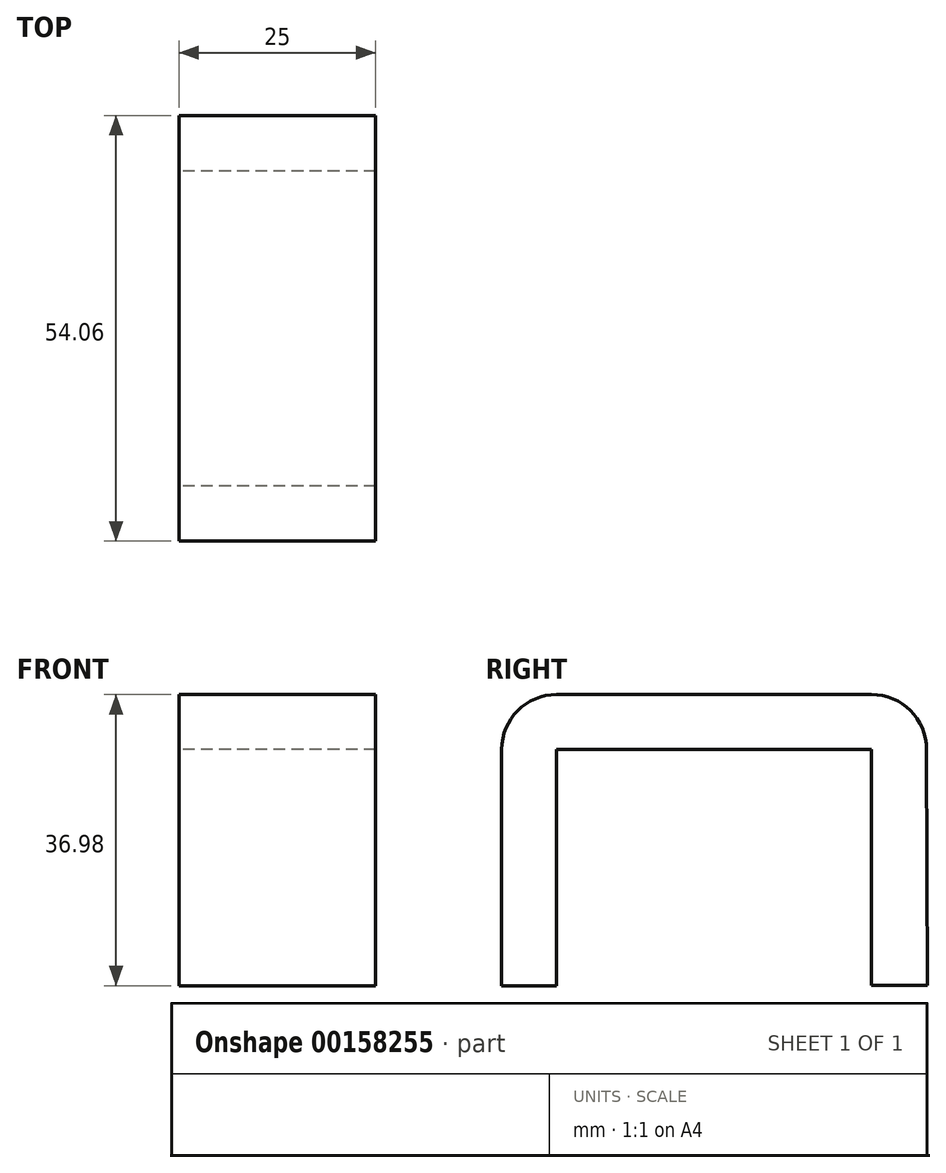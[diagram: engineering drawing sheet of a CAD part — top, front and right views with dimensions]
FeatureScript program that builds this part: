
annotation { "Feature Type Name" : "Feature", "Feature Type Description" : "" }
export const myFeature = defineFeature(function(context is Context, id is Id, definition is map)
    precondition{}
    {
        {
            var Q0;
            Q0=qCreatedBy(makeId("Right.planeOp"),FACE);
            var sketch = newSketch(context, id + "F0", { "sketchPlane" : qUnion([Q0])});
            skLineSegment(sketch, "E0", {"start": v(-27, 2.82) * mm, "end": v(-27, -27.18) * mm});
            skArc(sketch, "E1", {"start": v(-27, 2.82) * mm, "mid": v(-24.95, 7.76) * mm, "end": v(-20, 9.8) * mm});
            skLineSegment(sketch, "E2", {"start": v(-20, 9.8) * mm, "end": v(20, 9.8) * mm});
            skArc(sketch, "E3", {"start": v(20, 9.8) * mm, "mid": v(24.92, 7.76) * mm, "end": v(26.98, 2.84) * mm});
            skLineSegment(sketch, "E4", {"start": v(26.98, 2.84) * mm, "end": v(27.07, -27.16) * mm});
            skLineSegment(sketch, "E5", {"start": v(-27, -27.18) * mm, "end": v(-20, -27.18) * mm});
            skLineSegment(sketch, "E6", {"start": v(-20, -27.18) * mm, "end": v(-20, 2.82) * mm});
            skLineSegment(sketch, "E7", {"start": v(-20, 2.82) * mm, "end": v(20, 2.82) * mm});
            skLineSegment(sketch, "E8", {"start": v(20, 2.82) * mm, "end": v(20, -27.16) * mm});
            skLineSegment(sketch, "E9", {"start": v(20, -27.16) * mm, "end": v(27.07, -27.16) * mm});
            skSolve(sketch);
        }
        {
            var Q0;
            Q0=makeQuery(id+"F0.imprint","IMPRINT",FACE,{"disambiguationData":[TD([[makeQuery(id+"F0.imprint","IMPRINT",EDGE,{"derivedFrom":sQuery(id+"F0.wireOp",EDGE,"E0")}),1.0]])]});
            extrude(context, id + "F1", {"entities" : qUnion([Q0]), "depth" : 25 * mm});
        }
    });
